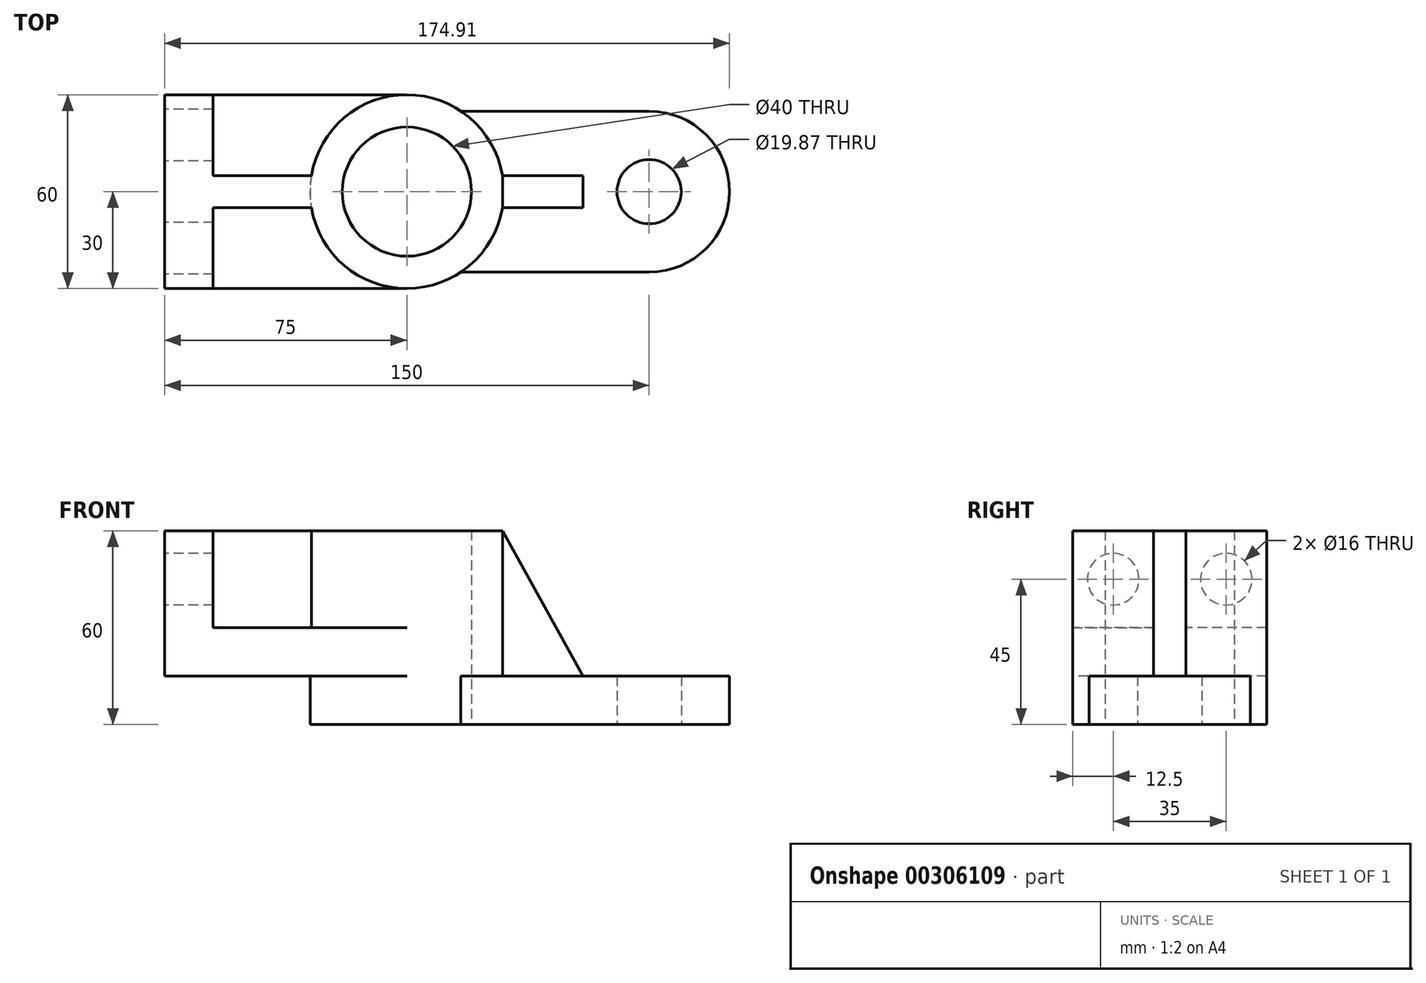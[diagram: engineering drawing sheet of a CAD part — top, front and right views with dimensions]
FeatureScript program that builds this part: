
annotation { "Feature Type Name" : "Feature", "Feature Type Description" : "" }
export const myFeature = defineFeature(function(context is Context, id is Id, definition is map)
    precondition{}
    {
        {
            var Q0;
            Q0=qCreatedBy(makeId("Top.planeOp"),FACE);
            var sketch = newSketch(context, id + "F0", { "sketchPlane" : qUnion([Q0])});
            skCircle(sketch, "E0", {"center": v(0, 0) * mm, "radius": 30 * mm});
            skCircle(sketch, "E1", {"center": v(0, 0) * mm, "radius": 20 * mm});
            skSolve(sketch);
        }
        {
            var Q0;
            Q0 = qSketchRegion(id + "F0", true);
            extrude(context, id + "F1", {"entities" : qUnion([Q0]), "depth" : 60 * mm});
        }
        {
            var Q0;
            Q0=qCreatedBy(makeId("Top.planeOp"),FACE);
            var sketch = newSketch(context, id + "F2", { "sketchPlane" : qUnion([Q0])});
            skCircle(sketch, "E2", {"center": v(75, 0) * mm, "radius": 9.94 * mm});
            skArc(sketch, "E3", {"start": v(75, -24.9) * mm, "mid": v(99.9, 0) * mm, "end": v(75, 24.9) * mm});
            skLineSegment(sketch, "E4", {"start": v(75, 24.9) * mm, "end": v(16.72, 24.9) * mm});
            skLineSegment(sketch, "E5", {"start": v(75, -24.9) * mm, "end": v(16.72, -24.9) * mm});
            skArc(sketch, "E6.0", {"start": v(16.72, 24.9) * mm, "mid": v(-30, 0) * mm, "end": v(16.72, -24.9) * mm});
            skCircle(sketch, "E7.0", {"center": v(0, 0) * mm, "radius": 20 * mm});
            skSolve(sketch);
        }
        {
            var Q0;
            Q0 = qSketchRegion(id + "F2", true);
            extrude(context, id + "F3", {"entities" : qUnion([Q0]), "operationType" : NewBodyOperationType.ADD, "depth" : 15 * mm});
        }
        {
            var Q0;
            Q0=makeQuery(id+"F3.opExtrude","CAP_FACE",FACE,{"disambiguationData":[OSD([sQuery(id+"F2.wireOp",EDGE,"E2"),sQuery(id+"F2.wireOp",EDGE,"E3"),sQuery(id+"F2.wireOp",EDGE,"E4"),sQuery(id+"F2.wireOp",EDGE,"E5"),sQuery(id+"F2.wireOp",EDGE,"E6.0"),sQuery(id+"F2.wireOp",EDGE,"E7.0")])],"isStart":false});
            var sketch = newSketch(context, id + "F4", { "sketchPlane" : qUnion([Q0])});
            skLineSegment(sketch, "E8", {"start": v(29.58, 5) * mm, "end": v(54.58, 5) * mm});
            skLineSegment(sketch, "E9", {"start": v(54.58, 5) * mm, "end": v(54.58, -5) * mm});
            skLineSegment(sketch, "E10", {"start": v(54.58, -5) * mm, "end": v(29.58, -5) * mm});
            skArc(sketch, "E11.0", {"start": v(29.58, -5) * mm, "mid": v(30, 0) * mm, "end": v(29.58, 5) * mm});
            skSolve(sketch);
        }
        {
            var Q0;
            Q0 = qSketchRegion(id + "F4", true);
            var Q1;
            Q1=makeQuery(id+"F1.opExtrude","CAP_FACE",FACE,{"disambiguationData":[OSD([sQuery(id+"F0.wireOp",EDGE,"E0"),sQuery(id+"F0.wireOp",EDGE,"E1")])],"isStart":false});
            extrude(context, id + "F5", {"entities" : qUnion([Q0]), "operationType" : NewBodyOperationType.ADD, "endBound" : BoundingType.UP_TO_SURFACE, "endBoundEntityFace" : qUnion([Q1]), "depth" : 25 * mm});
        }
        {
            var Q0;
            Q0=makeQuery(id+"F5.opExtrude","CAP_EDGE",EDGE,{"disambiguationData":[OSD([sQuery(id+"F4.wireOp",EDGE,"E9")])],"isStart":false});
            chamfer(context, id + "F6", {"entities" : qUnion([Q0]), "chamferType" : ChamferType.TWO_OFFSETS, "width1" : 45 * mm, "oppositeDirection" : false, "width2" : 25 * mm});
        }
        {
            var Q0;
            Q0=makeQuery(id+"F3.opExtrude","CAP_FACE",FACE,{"disambiguationData":[OSD([sQuery(id+"F2.wireOp",EDGE,"E2"),sQuery(id+"F2.wireOp",EDGE,"E3"),sQuery(id+"F2.wireOp",EDGE,"E4"),sQuery(id+"F2.wireOp",EDGE,"E5"),sQuery(id+"F2.wireOp",EDGE,"E6.0"),sQuery(id+"F2.wireOp",EDGE,"E7.0")])],"isStart":false});
            var sketch = newSketch(context, id + "F7", { "sketchPlane" : qUnion([Q0])});
            skArc(sketch, "E12.0", {"start": v(29.58, 5) * mm, "mid": v(-30, 0) * mm, "end": v(29.58, -5) * mm});
            skCircle(sketch, "E13.0", {"center": v(0, 0) * mm, "radius": 20 * mm});
            skLineSegment(sketch, "E14", {"start": v(0, 30) * mm, "end": v(-75, 30) * mm});
            skLineSegment(sketch, "E15", {"start": v(-75, 30) * mm, "end": v(-75, -30) * mm});
            skLineSegment(sketch, "E16", {"start": v(-75, -30) * mm, "end": v(0, -30) * mm});
            skLineSegment(sketch, "E17.0", {"start": v(29.58, -5) * mm, "end": v(29.58, 5) * mm});
            skSolve(sketch);
        }
        {
            var Q0;
            Q0 = qSketchRegion(id + "F7", true);
            extrude(context, id + "F8", {"entities" : qUnion([Q0]), "operationType" : NewBodyOperationType.ADD, "depth" : 15 * mm});
        }
        {
            var Q0;
            Q0=makeQuery(id+"F8.opExtrude","CAP_FACE",FACE,{"disambiguationData":[OSD([sQuery(id+"F7.wireOp",EDGE,"E13.0"),sQuery(id+"F7.wireOp",EDGE,"E14"),sQuery(id+"F7.wireOp",EDGE,"E15"),sQuery(id+"F7.wireOp",EDGE,"E16"),sQuery(id+"F7.wireOp",EDGE,"E12.0"),sQuery(id+"F7.wireOp",EDGE,"E17.0")])],"isStart":false});
            var sketch = newSketch(context, id + "F9", { "sketchPlane" : qUnion([Q0])});
            skLineSegment(sketch, "E18", {"start": v(-75, 30) * mm, "end": v(-75, -30) * mm});
            skLineSegment(sketch, "E19", {"start": v(-75, -30) * mm, "end": v(-60, -30) * mm});
            skLineSegment(sketch, "E20", {"start": v(-60, -30) * mm, "end": v(-60, -5) * mm});
            skLineSegment(sketch, "E21", {"start": v(-60, -5) * mm, "end": v(-29.58, -5) * mm});
            skArc(sketch, "E22.0", {"start": v(-29.58, 5) * mm, "mid": v(-30, 0) * mm, "end": v(-29.58, -5) * mm});
            skLineSegment(sketch, "E23", {"start": v(-75, 30) * mm, "end": v(-60, 30) * mm});
            skLineSegment(sketch, "E24", {"start": v(-60, 30) * mm, "end": v(-60, 5) * mm});
            skLineSegment(sketch, "E25", {"start": v(-60, 5) * mm, "end": v(-29.58, 5) * mm});
            skPoint(sketch, "E26.orphan", {"position": v(29.58, 5) * mm});
            skPoint(sketch, "E27.orphan", {"position": v(29.58, -5) * mm});
            skSolve(sketch);
        }
        {
            var Q0;
            Q0 = qSketchRegion(id + "F9", true);
            var Q1;
            Q1=makeQuery(id+"F5.boolean.opBoolean","MERGE",FACE,{"derivedFrom":[makeQuery(id+"F1.opExtrude","CAP_FACE",FACE,{"disambiguationData":[OSD([sQuery(id+"F0.wireOp",EDGE,"E0"),sQuery(id+"F0.wireOp",EDGE,"E1")])],"isStart":false}),makeQuery(id+"F5.opExtrude","CAP_FACE",FACE,{"disambiguationData":[OSD([sQuery(id+"F4.wireOp",EDGE,"E8"),sQuery(id+"F4.wireOp",EDGE,"E9"),sQuery(id+"F4.wireOp",EDGE,"E10"),sQuery(id+"F4.wireOp",EDGE,"E11.0")])],"isStart":false})]});
            extrude(context, id + "F10", {"entities" : qUnion([Q0]), "operationType" : NewBodyOperationType.ADD, "endBound" : BoundingType.UP_TO_SURFACE, "endBoundEntityFace" : qUnion([Q1]), "depth" : 25 * mm});
        }
        {
            var Q0;
            Q0=makeQuery(id+"F10.boolean.opBoolean","MERGE",FACE,{"derivedFrom":[makeQuery(id+"F8.opExtrude","SWEPT_FACE",FACE,{"disambiguationData":[OSD([sQuery(id+"F7.wireOp",EDGE,"E15")])]}),makeQuery(id+"F10.opExtrude","SWEPT_FACE",FACE,{"disambiguationData":[OSD([sQuery(id+"F9.wireOp",EDGE,"E18")])]})]});
            var sketch = newSketch(context, id + "F11", { "sketchPlane" : qUnion([Q0])});
            skCircle(sketch, "E28", {"center": v(17.5, 45) * mm, "radius": 8 * mm});
            skCircle(sketch, "E29", {"center": v(-17.5, 45) * mm, "radius": 8 * mm});
            skSolve(sketch);
        }
        {
            var Q0;
            Q0 = qSketchRegion(id + "F11", true);
            var Q1;
            Q1=makeQuery(id+"F10.opExtrude","SWEPT_FACE",FACE,{"disambiguationData":[OSD([sQuery(id+"F9.wireOp",EDGE,"E20")])]});
            extrude(context, id + "F12", {"entities" : qUnion([Q0]), "operationType" : NewBodyOperationType.REMOVE, "endBound" : BoundingType.UP_TO_SURFACE, "oppositeDirection" : true, "endBoundEntityFace" : qUnion([Q1]), "depth" : 25 * mm});
        }
    });
